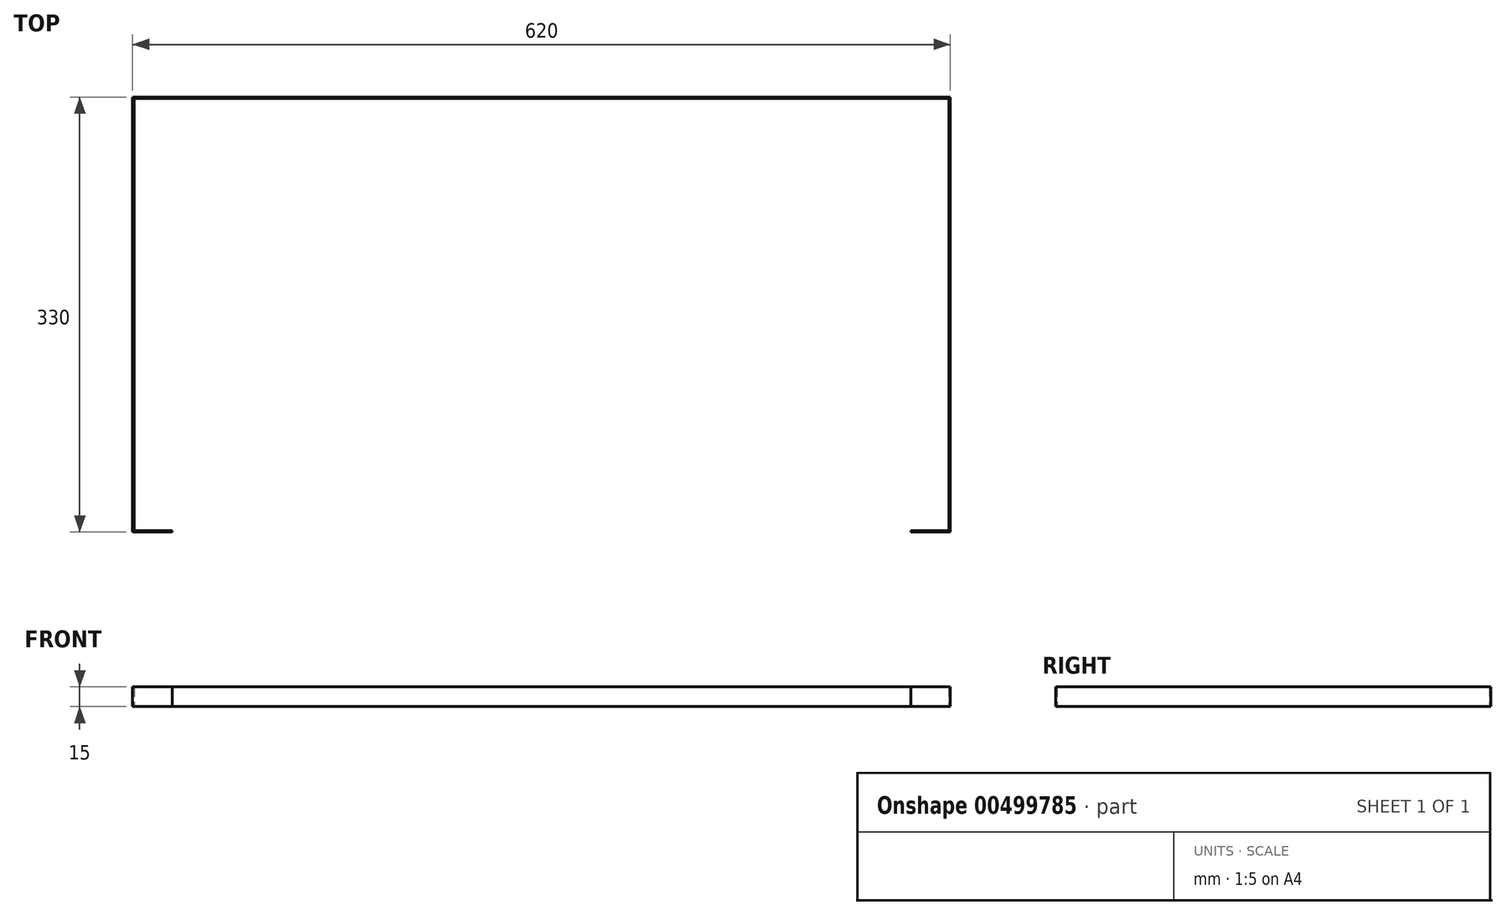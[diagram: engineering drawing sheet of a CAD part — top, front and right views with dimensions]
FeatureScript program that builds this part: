
annotation { "Feature Type Name" : "Feature", "Feature Type Description" : "" }
export const myFeature = defineFeature(function(context is Context, id is Id, definition is map)
    precondition{}
    {
        {
            var Q0;
            Q0=qCreatedBy(makeId("Top.planeOp"),FACE);
            var sketch = newSketch(context, id + "F0", { "sketchPlane" : qUnion([Q0])});
            skLineSegment(sketch, "E0", {"start": v(-71.1, -174.57) * mm, "end": v(-71.1, 155.43) * mm});
            skLineSegment(sketch, "E1", {"start": v(-71.1, 155.43) * mm, "end": v(548.9, 155.43) * mm});
            skLineSegment(sketch, "E2", {"start": v(548.9, 155.43) * mm, "end": v(548.9, -174.57) * mm});
            skLineSegment(sketch, "E3", {"start": v(548.9, -174.57) * mm, "end": v(518.9, -174.57) * mm});
            skLineSegment(sketch, "E4", {"start": v(-71.1, -174.57) * mm, "end": v(-41.1, -174.57) * mm});
            skLineSegment(sketch, "E5", {"start": v(-41.1, -174.57) * mm, "end": v(-41.1, -173.57) * mm});
            skLineSegment(sketch, "E6", {"start": v(-70.1, -173.57) * mm, "end": v(-41.1, -173.57) * mm});
            skLineSegment(sketch, "E7", {"start": v(-70.1, 154.43) * mm, "end": v(-70.1, -173.57) * mm});
            skLineSegment(sketch, "E8", {"start": v(547.9, 154.43) * mm, "end": v(-70.1, 154.43) * mm});
            skLineSegment(sketch, "E9", {"start": v(547.9, -173.57) * mm, "end": v(547.9, 154.43) * mm});
            skLineSegment(sketch, "E10", {"start": v(518.9, -173.57) * mm, "end": v(547.9, -173.57) * mm});
            skLineSegment(sketch, "E11", {"start": v(518.9, -174.57) * mm, "end": v(518.9, -173.57) * mm});
            skSolve(sketch);
        }
        {
            var Q0;
            Q0 = qSketchRegion(id + "F0", true);
            extrude(context, id + "F1", {"entities" : qUnion([Q0]), "depth" : 15 * mm});
        }
    });
